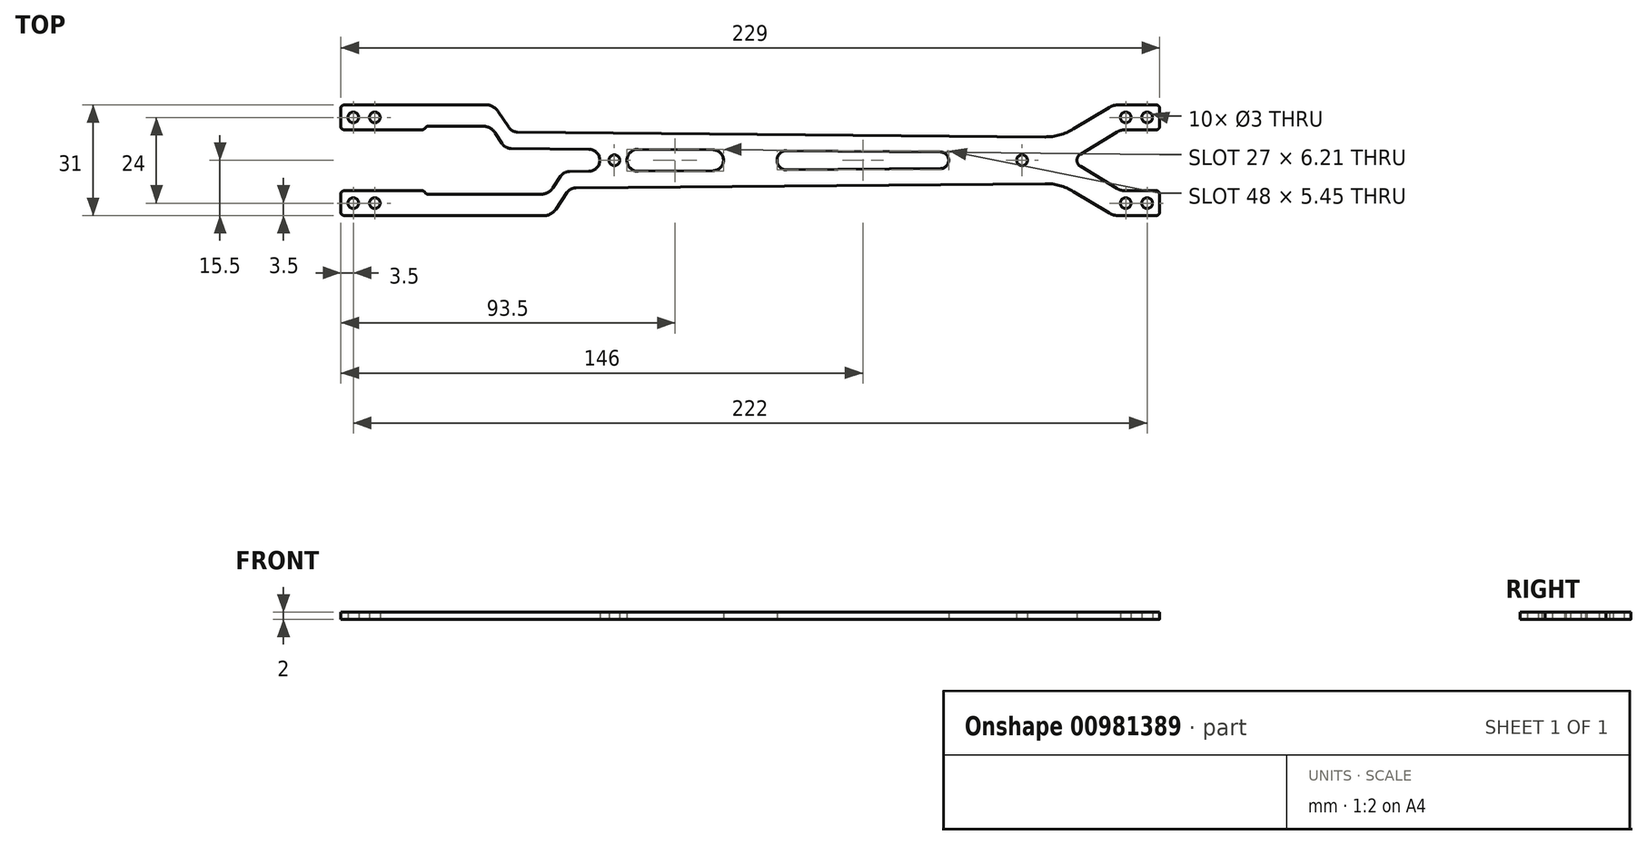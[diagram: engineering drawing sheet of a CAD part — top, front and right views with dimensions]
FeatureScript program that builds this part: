
annotation { "Feature Type Name" : "Feature", "Feature Type Description" : "" }
export const myFeature = defineFeature(function(context is Context, id is Id, definition is map)
    precondition{}
    {
        {
            var Q0;
            Q0=qCreatedBy(makeId("Top.planeOp"),FACE);
            var sketch = newSketch(context, id + "F0", { "sketchPlane" : qUnion([Q0])});
            skCircle(sketch, "E0", {"center": v(-91.08, -12) * mm, "radius": 1.5 * mm});
            skCircle(sketch, "E1", {"center": v(130.92, -12) * mm, "radius": 1.5 * mm});
            skCircle(sketch, "E2", {"center": v(-85.08, -12) * mm, "radius": 1.5 * mm});
            skCircle(sketch, "E3", {"center": v(-91.08, 12) * mm, "radius": 1.5 * mm});
            skCircle(sketch, "E4", {"center": v(-85.08, 12) * mm, "radius": 1.5 * mm});
            skCircle(sketch, "E5", {"center": v(130.92, 12) * mm, "radius": 1.5 * mm});
            skCircle(sketch, "E6", {"center": v(124.92, 12) * mm, "radius": 1.5 * mm});
            skCircle(sketch, "E7", {"center": v(124.92, -12) * mm, "radius": 1.5 * mm});
            skCircle(sketch, "E8", {"center": v(95.92, 0) * mm, "radius": 1.5 * mm});
            skCircle(sketch, "E9", {"center": v(-18.08, 0) * mm, "radius": 1.5 * mm});
            skLineSegment(sketch, "E10", {"start": v(-94.58, -14.5) * mm, "end": v(-94.58, -9.5) * mm});
            skLineSegment(sketch, "E11", {"start": v(-93.58, -8.5) * mm, "end": v(-72, -8.5) * mm});
            skLineSegment(sketch, "E12", {"start": v(-93.58, -15.5) * mm, "end": v(-37.78, -15.5) * mm});
            skLineSegment(sketch, "E13", {"start": v(122.86, -15.5) * mm, "end": v(133.42, -15.5) * mm});
            skLineSegment(sketch, "E14", {"start": v(134.42, -14.5) * mm, "end": v(134.42, -9.5) * mm});
            skLineSegment(sketch, "E15", {"start": v(133.42, -8.5) * mm, "end": v(124.54, -8.5) * mm});
            skLineSegment(sketch, "E16", {"start": v(122.46, -7.92) * mm, "end": v(112.24, -1.7) * mm});
            skLineSegment(sketch, "E17.0", {"start": v(120.27, -14.77) * mm, "end": v(110.29, -8.72) * mm});
            skLineSegment(sketch, "E18", {"start": v(102.37, -6.54) * mm, "end": v(-28.88, -7.74) * mm});
            skLineSegment(sketch, "E19", {"start": v(-34.46, -13.73) * mm, "end": v(-31.34, -9.07) * mm});
            skLineSegment(sketch, "E20", {"start": v(-30.62, -3.15) * mm, "end": v(-25.21, -3.1) * mm});
            skLineSegment(sketch, "E21", {"start": v(-35.26, -7.73) * mm, "end": v(-33.08, -4.48) * mm});
            skLineSegment(sketch, "E22.MirrorCS", {"start": v(122.46, 7.92) * mm, "end": v(112.24, 1.7) * mm});
            skLineSegment(sketch, "E23.MirrorCS", {"start": v(133.42, 8.5) * mm, "end": v(124.54, 8.5) * mm});
            skLineSegment(sketch, "E24.MirrorCS", {"start": v(-93.58, 15.5) * mm, "end": v(-53.96, 15.5) * mm});
            skLineSegment(sketch, "E25.MirrorCS", {"start": v(134.42, 14.5) * mm, "end": v(134.42, 9.5) * mm});
            skLineSegment(sketch, "E26.MirrorCS", {"start": v(120.27, 14.77) * mm, "end": v(110.29, 8.72) * mm});
            skLineSegment(sketch, "E27.MirrorCS", {"start": v(122.86, 15.5) * mm, "end": v(133.42, 15.5) * mm});
            skLineSegment(sketch, "E28.MirrorCS", {"start": v(102.37, 6.54) * mm, "end": v(-45.15, 7.89) * mm});
            skLineSegment(sketch, "E29", {"start": v(-47.62, 9.22) * mm, "end": v(-50.64, 13.73) * mm});
            skLineSegment(sketch, "E30", {"start": v(-94.58, 14.5) * mm, "end": v(-94.58, 9.5) * mm});
            skLineSegment(sketch, "E31", {"start": v(-11.45, -3.1) * mm, "end": v(9.54, -2.91) * mm});
            skLineSegment(sketch, "E32.MirrorCS", {"start": v(-11.45, 3.1) * mm, "end": v(9.54, 2.91) * mm});
            skArc(sketch, "E33", {"start": v(-11.45, 3.1) * mm, "mid": v(-14.58, 0) * mm, "end": v(-11.45, -3.1) * mm});
            skArc(sketch, "E34", {"start": v(73.11, -2.33) * mm, "mid": v(75.42, 0) * mm, "end": v(73.11, 2.33) * mm});
            skLineSegment(sketch, "E35.trimOffspring", {"start": v(30.17, -2.72) * mm, "end": v(73.11, -2.33) * mm});
            skLineSegment(sketch, "E36.trimOffspring", {"start": v(30.17, 2.72) * mm, "end": v(73.11, 2.33) * mm});
            skArc(sketch, "E37", {"start": v(9.54, -2.91) * mm, "mid": v(12.42, 0) * mm, "end": v(9.54, 2.91) * mm});
            skArc(sketch, "E38", {"start": v(30.17, 2.72) * mm, "mid": v(27.42, 0) * mm, "end": v(30.17, -2.72) * mm});
            skLineSegment(sketch, "E39", {"start": v(-70.17, -9.5) * mm, "end": v(-38.58, -9.5) * mm});
            skLineSegment(sketch, "E40", {"start": v(-33.08, -4.48) * mm, "end": v(-35.26, -7.73) * mm});
            skLineSegment(sketch, "E41.MirrorCS", {"start": v(-70.17, 9.5) * mm, "end": v(-54.76, 9.5) * mm});
            skLineSegment(sketch, "E42", {"start": v(-70.87, -9.2) * mm, "end": v(-71.29, -8.8) * mm});
            skLineSegment(sketch, "E43.MirrorCS", {"start": v(-70.87, 9.2) * mm, "end": v(-71.29, 8.8) * mm});
            skLineSegment(sketch, "E44.MirrorCS", {"start": v(-93.58, 8.5) * mm, "end": v(-72, 8.5) * mm});
            skArc(sketch, "E45.filletArc", {"start": v(-70.87, -9.2) * mm, "mid": v(-70.55, -9.42) * mm, "end": v(-70.17, -9.5) * mm});
            skArc(sketch, "E46.filletArc", {"start": v(-71.29, -8.8) * mm, "mid": v(-71.61, -8.58) * mm, "end": v(-72, -8.5) * mm});
            skArc(sketch, "E47.filletArc", {"start": v(-70.17, 9.5) * mm, "mid": v(-70.55, 9.42) * mm, "end": v(-70.87, 9.2) * mm});
            skArc(sketch, "E48.filletArc", {"start": v(-72, 8.5) * mm, "mid": v(-71.61, 8.58) * mm, "end": v(-71.29, 8.8) * mm});
            skArc(sketch, "E49.filletArc", {"start": v(-38.58, -9.5) * mm, "mid": v(-36.7, -9.03) * mm, "end": v(-35.26, -7.73) * mm});
            skArc(sketch, "E50.filletArc", {"start": v(-51.4, 7.67) * mm, "mid": v(-52.84, 9.01) * mm, "end": v(-54.76, 9.5) * mm});
            skArc(sketch, "E51.filletArc", {"start": v(-30.62, -3.15) * mm, "mid": v(-32.02, -3.51) * mm, "end": v(-33.08, -4.48) * mm});
            skArc(sketch, "E52.filletArc", {"start": v(-47.62, 9.22) * mm, "mid": v(-46.55, 8.25) * mm, "end": v(-45.15, 7.89) * mm});
            skArc(sketch, "E53.filletArc", {"start": v(-28.88, -7.74) * mm, "mid": v(-30.27, -8.1) * mm, "end": v(-31.34, -9.07) * mm});
            skArc(sketch, "E54.filletArc", {"start": v(-50.64, 13.73) * mm, "mid": v(-52.08, 15.03) * mm, "end": v(-53.96, 15.5) * mm});
            skArc(sketch, "E55.filletArc", {"start": v(-37.78, -15.5) * mm, "mid": v(-35.9, -15.03) * mm, "end": v(-34.46, -13.73) * mm});
            skArc(sketch, "E56.filletArc", {"start": v(-94.58, -14.5) * mm, "mid": v(-94.29, -15.2) * mm, "end": v(-93.58, -15.5) * mm});
            skArc(sketch, "E57.filletArc", {"start": v(-93.58, -8.5) * mm, "mid": v(-94.29, -8.8) * mm, "end": v(-94.58, -9.5) * mm});
            skArc(sketch, "E58.filletArc", {"start": v(-94.58, 9.5) * mm, "mid": v(-94.29, 8.8) * mm, "end": v(-93.58, 8.5) * mm});
            skArc(sketch, "E59.filletArc", {"start": v(-93.58, 15.5) * mm, "mid": v(-94.29, 15.2) * mm, "end": v(-94.58, 14.5) * mm});
            skPoint(sketch, "E60.visualSharp", {"position": v(134.42, 15.5) * mm});
            skArc(sketch, "E60.filletArc", {"start": v(134.42, 14.5) * mm, "mid": v(134.13, 15.2) * mm, "end": v(133.42, 15.5) * mm});
            skPoint(sketch, "E61.visualSharp", {"position": v(134.42, 8.5) * mm});
            skArc(sketch, "E61.filletArc", {"start": v(133.42, 8.5) * mm, "mid": v(134.13, 8.8) * mm, "end": v(134.42, 9.5) * mm});
            skPoint(sketch, "E62.visualSharp", {"position": v(134.42, -8.5) * mm});
            skArc(sketch, "E62.filletArc", {"start": v(134.42, -9.5) * mm, "mid": v(134.13, -8.8) * mm, "end": v(133.42, -8.5) * mm});
            skPoint(sketch, "E63.visualSharp", {"position": v(134.42, -15.5) * mm});
            skArc(sketch, "E63.filletArc", {"start": v(133.42, -15.5) * mm, "mid": v(134.13, -15.2) * mm, "end": v(134.42, -14.5) * mm});
            skPoint(sketch, "E64.visualSharp", {"position": v(123.42, 8.5) * mm});
            skArc(sketch, "E64.filletArc", {"start": v(124.54, 8.5) * mm, "mid": v(123.46, 8.35) * mm, "end": v(122.46, 7.92) * mm});
            skPoint(sketch, "E65.visualSharp", {"position": v(123.42, -8.5) * mm});
            skArc(sketch, "E65.filletArc", {"start": v(122.46, -7.92) * mm, "mid": v(123.46, -8.35) * mm, "end": v(124.54, -8.5) * mm});
            skPoint(sketch, "E66.visualSharp", {"position": v(121.46, 15.5) * mm});
            skArc(sketch, "E66.filletArc", {"start": v(122.86, 15.5) * mm, "mid": v(121.51, 15.32) * mm, "end": v(120.27, 14.77) * mm});
            skPoint(sketch, "E67.visualSharp", {"position": v(121.46, -15.5) * mm});
            skArc(sketch, "E67.filletArc", {"start": v(120.27, -14.77) * mm, "mid": v(121.51, -15.32) * mm, "end": v(122.86, -15.5) * mm});
            skPoint(sketch, "E68.visualSharp", {"position": v(106.64, -6.5) * mm});
            skArc(sketch, "E68.filletArc", {"start": v(110.29, -8.72) * mm, "mid": v(106.48, -7.07) * mm, "end": v(102.37, -6.54) * mm});
            skPoint(sketch, "E69.visualSharp", {"position": v(106.64, 6.5) * mm});
            skArc(sketch, "E69.filletArc", {"start": v(102.37, 6.54) * mm, "mid": v(106.48, 7.07) * mm, "end": v(110.29, 8.72) * mm});
            skPoint(sketch, "E70.visualSharp", {"position": v(109.42, 0) * mm});
            skArc(sketch, "E70.filletArc", {"start": v(112.24, 1.7) * mm, "mid": v(111.27, 0) * mm, "end": v(112.24, -1.7) * mm});
            skLineSegment(sketch, "E71.MirrorCS", {"start": v(-46.97, 3.3) * mm, "end": v(-25.21, 3.1) * mm});
            skArc(sketch, "E72.MirrorCS", {"start": v(-46.97, 3.3) * mm, "mid": v(-48.38, 3.67) * mm, "end": v(-49.46, 4.67) * mm});
            skArc(sketch, "E73", {"start": v(-25.21, -3.1) * mm, "mid": v(-22.14, 0) * mm, "end": v(-25.21, 3.1) * mm});
            skLineSegment(sketch, "E74", {"start": v(-49.46, 4.67) * mm, "end": v(-51.4, 7.67) * mm});
            skSolve(sketch);
        }
        {
            var Q0;
            Q0=makeQuery(id+"F0.imprint","IMPRINT",FACE,{"disambiguationData":[TD([[makeQuery(id+"F0.imprint","IMPRINT",EDGE,{"derivedFrom":sQuery(id+"F0.wireOp",EDGE,"E0")}),-1.0]])]});
            extrude(context, id + "F1", {"entities" : qUnion([Q0]), "depth" : 2 * mm, "offsetDistance" : 25 * mm});
        }
    });
